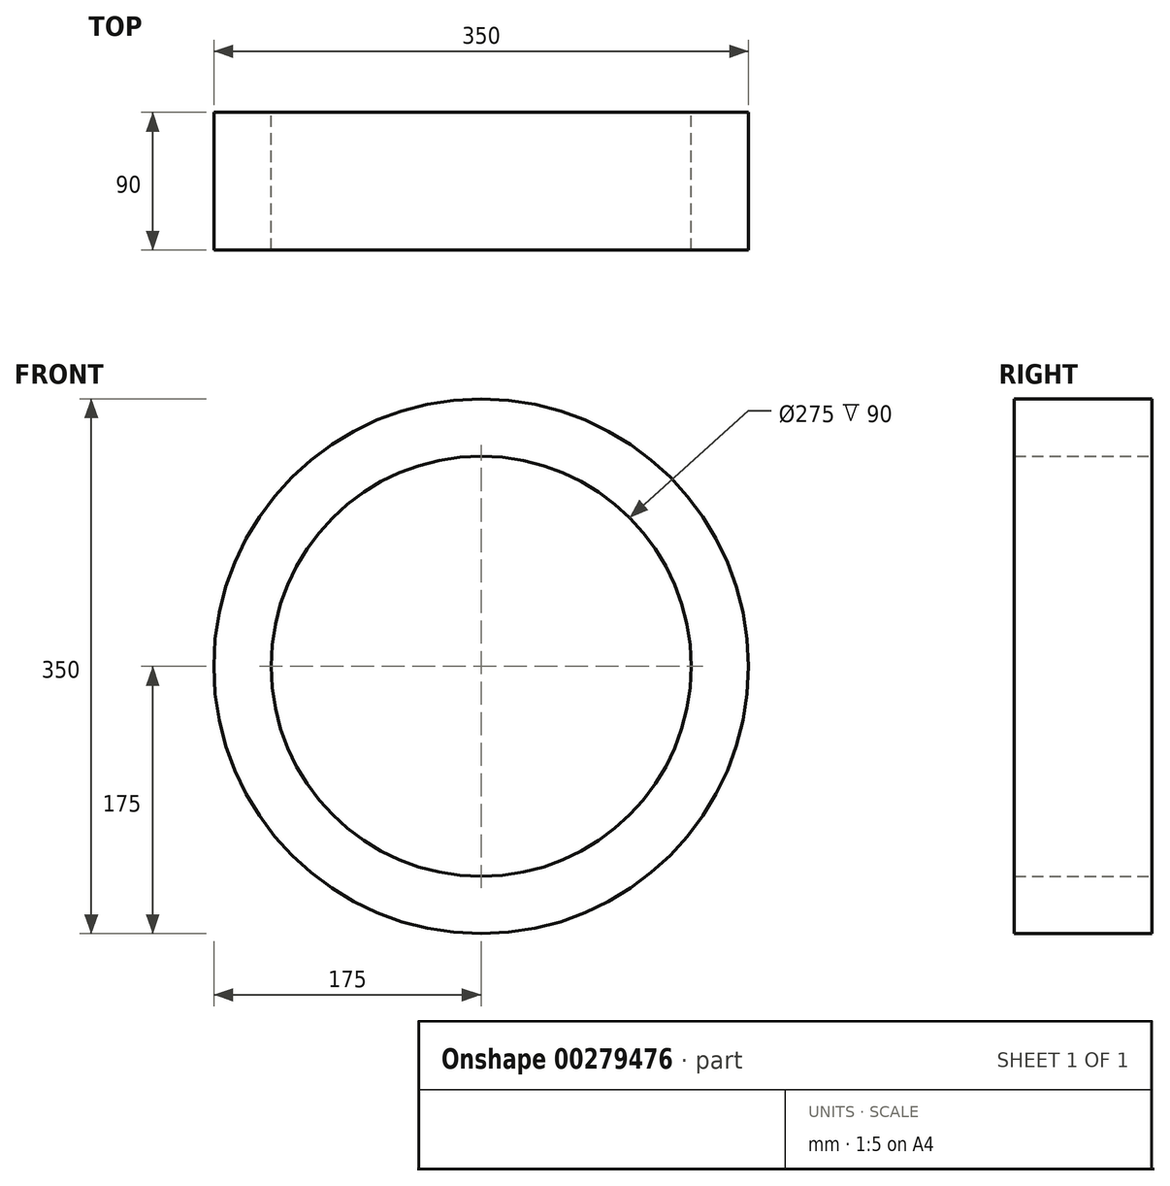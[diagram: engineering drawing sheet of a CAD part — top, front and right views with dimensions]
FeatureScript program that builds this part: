
annotation { "Feature Type Name" : "Feature", "Feature Type Description" : "" }
export const myFeature = defineFeature(function(context is Context, id is Id, definition is map)
    precondition{}
    {
        {
            var Q0;
            Q0=qCreatedBy(makeId("Front.planeOp"),FACE);
            var sketch = newSketch(context, id + "F0", { "sketchPlane" : qUnion([Q0])});
            skCircle(sketch, "E0", {"center": v(0, 0) * mm, "radius": 175 * mm});
            skSolve(sketch);
        }
        {
            var Q0;
            Q0=makeQuery(id+"F0.imprint","IMPRINT",FACE,{"disambiguationData":[TD([[makeQuery(id+"F0.imprint","IMPRINT",EDGE,{"derivedFrom":sQuery(id+"F0.wireOp",EDGE,"E0")}),1.0]])]});
            var sketch = newSketch(context, id + "F1", { "sketchPlane" : qUnion([Q0])});
            skCircle(sketch, "E1", {"center": v(0, 0) * mm, "radius": 137.5 * mm});
            skSolve(sketch);
        }
        {
            var Q0;
            Q0=makeQuery(id+"F0.imprint","IMPRINT",FACE,{"disambiguationData":[TD([[makeQuery(id+"F0.imprint","IMPRINT",EDGE,{"derivedFrom":sQuery(id+"F0.wireOp",EDGE,"E0")}),1.0]])]});
            extrude(context, id + "F2", {"entities" : qUnion([Q0]), "depth" : 90 * mm, "offsetDistance" : 25 * mm});
        }
        {
            var Q0;
            Q0=makeQuery(id+"F1.imprint","IMPRINT",FACE,{"disambiguationData":[TD([[makeQuery(id+"F1.imprint","IMPRINT",EDGE,{"derivedFrom":sQuery(id+"F1.wireOp",EDGE,"E1")}),1.0]])]});
            extrude(context, id + "F3", {"entities" : qUnion([Q0]), "operationType" : NewBodyOperationType.REMOVE, "depth" : 241 * mm, "offsetDistance" : 25 * mm});
        }
    });
